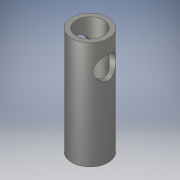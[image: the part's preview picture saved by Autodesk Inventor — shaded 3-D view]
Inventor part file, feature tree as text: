
AUTODESK INVENTOR PART (.ipt)
format: ipt  version: 2018 (Build 220112000, 112)  size: 130,048 bytes
history: native  units: in
note: dims shown in document units (in); Inventor stores cm internally (conversion verified against a paired STEP export)
features: extrude x3, sketch x3
ambient origin geometry x8: Origin, YZ Plane, XZ Plane, XY Plane, X Axis, Y Axis, Z Axis, Center Point
bodies: Solid1 (feature_tree)
feature tree (6):
  extrude  "Extrusion1"  Depth=1.476in TaperAngle=0.0deg
  extrude  "Extrusion3"  Depth=1.25in TaperAngle=0.0deg
  extrude  "Extrusion4"  Depth=1.133in
  sketch  "Sketch1"  dims[d0=0.5in d1=1.476in d2=0.5in d3=0.0in d4=0.0in]
  sketch  "Sketch3"  dims[d10=0.375in d11=1.25in d12=0.0in]
  sketch  "Sketch4"  dims[d13=0.312in d14=1.133in d15=0.25in d16=1.0in d17=0.0in]
